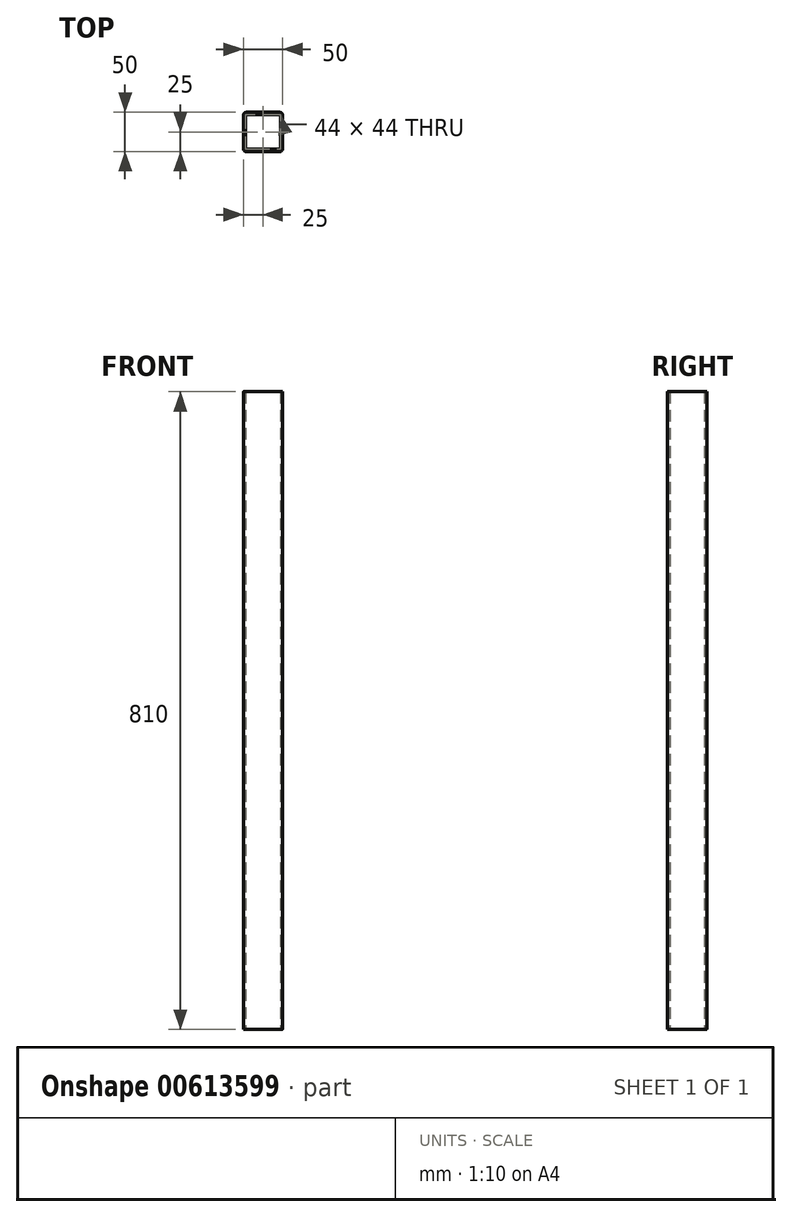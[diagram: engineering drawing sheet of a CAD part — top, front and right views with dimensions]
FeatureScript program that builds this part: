
annotation { "Feature Type Name" : "Feature", "Feature Type Description" : "" }
export const myFeature = defineFeature(function(context is Context, id is Id, definition is map)
    precondition{}
    {
        {
            var Q0;
            Q0=qCreatedBy(makeId("Top.planeOp"),FACE);
            var sketch = newSketch(context, id + "F0", { "sketchPlane" : qUnion([Q0])});
            skLineSegment(sketch, "E0.bottom", {"start": v(4, 0) * mm, "end": v(46, 0) * mm});
            skLineSegment(sketch, "E0.top", {"start": v(4, 50) * mm, "end": v(46, 50) * mm});
            skLineSegment(sketch, "E0.left", {"start": v(0, 4) * mm, "end": v(0, 46) * mm});
            skLineSegment(sketch, "E0.right", {"start": v(50, 4) * mm, "end": v(50, 46) * mm});
            skPoint(sketch, "E1.visualSharp", {"position": v(50, 0) * mm});
            skArc(sketch, "E1.filletArc", {"start": v(46, 0) * mm, "mid": v(48.83, 1.17) * mm, "end": v(50, 4) * mm});
            skPoint(sketch, "E2.visualSharp", {"position": v(50, 50) * mm});
            skArc(sketch, "E2.filletArc", {"start": v(50, 46) * mm, "mid": v(48.83, 48.83) * mm, "end": v(46, 50) * mm});
            skPoint(sketch, "E3.visualSharp", {"position": v(0, 50) * mm});
            skArc(sketch, "E3.filletArc", {"start": v(4, 50) * mm, "mid": v(1.17, 48.83) * mm, "end": v(0, 46) * mm});
            skPoint(sketch, "E4.visualSharp", {"position": v(0, 0) * mm});
            skArc(sketch, "E4.filletArc", {"start": v(0, 4) * mm, "mid": v(1.17, 1.17) * mm, "end": v(4, 0) * mm});
            skLineSegment(sketch, "E5.0", {"start": v(3, 47) * mm, "end": v(47, 47) * mm});
            skLineSegment(sketch, "E5.1", {"start": v(3, 3) * mm, "end": v(3, 47) * mm});
            skLineSegment(sketch, "E5.2", {"start": v(3, 3) * mm, "end": v(47, 3) * mm});
            skLineSegment(sketch, "E5.3", {"start": v(47, 3) * mm, "end": v(47, 47) * mm});
            skSolve(sketch);
        }
        {
            var Q0;
            Q0=qSketchRegion(id+"F0",true);
            extrude(context, id + "F1", {"entities" : qUnion([Q0]), "depth" : 810 * mm, "offsetDistance" : 25 * mm});
        }
    });
